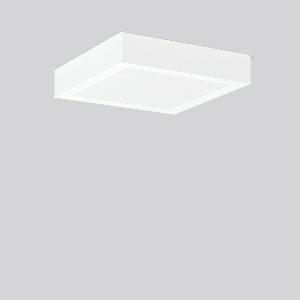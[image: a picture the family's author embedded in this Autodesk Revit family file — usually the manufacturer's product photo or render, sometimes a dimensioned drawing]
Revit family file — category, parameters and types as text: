
# Revit family: toledo_flat_square_a_672269_002_a995
name_source: partatom
category: Lighting Fixtures
units: mm (PartAtom-declared; Revit-internal decimal feet)

## family parameters
Cut with Voids When Loaded = No
Host = Face
Light Source = No
Part Type = Normal
Room Calculation Point = No
Round Connector Dimension = Use Diameter
Shared = No

## types (1)
- TOLEDO FLAT square A (1 x LED Modul 830, 2050 lm, 3000)
    Apparent Load = 22 VA
    CIE Flux Codes = 48 80 96 100 100
    Color Rendering = 80
    Color Temperature = 3000
    Default Elevation = 1800 mm
    Description = Series: TOLEDO FLAT square
Ultra thin surface mounted downlight. For escape route illumination. Surface mounted housing: sheet steel, powder-coated. Square cover plate: die-cast aluminium, powder coated. Light guide and diffuser made of non-yellowing PMMA, opal matt. Driver integrated. Suitable for connection to central battery systems. 
Colour: white
Length: 300 mm
Width: 300 mm
Height: 58 mm
Weight: 3.59 kg
Operating mode: maintained power mode
Lamp: LED
Socket: without socket
Colour temperature: 3000K
Colour rendering index (CRI): 80
System power: 22 W
Rated luminous flux: 2050 lm
Luminous flux, emergency: 2050 lm
System power, emergency: 22 W
Control gear: Regulated power supply
Protection class: I
Type of protection: IP 40
    Height = 58 mm
    Lamp = 1 x LED Modul 830
    Lamp Light Flux = 2050 lm
    Lamp count = 1
    Length = 300 mm
    Lifetime = 50000 h
    Luminous efficacy = 93 lm/W
    Manufacturer = RZB
    ModVariant = No
    Model = 672269.002
    Mounting Place = Ceiling
    Mounting Type = Surface mounted
    Number of Poles = 1
    OnlyDefault = Yes
    Power Factor = 1
    Product Name = TOLEDO FLAT square A
    Product group = Surface mounted downlights
    ProductGroupID = 302
    Protection Class = Protection class I
    Protection Degree = IP 40
    RLX_Detail_Level = 1
    RLX_Emergency_Light_Flux = 2050 lm
    RLX_Emergency_Type = 3
    RLX_Emergency_Type_DB = Yes
    RlxData = <blob elided: 13553 chars, md5=b06c832a>
    Socket = socket
    Standby Power = 0 W
    System Light Flux = 2050 lm
    System Power = 22 W
    Type Comments = Product without accessories
    Type Image = 901554.002.jpg
    URL = http://relux.com
    VarID = ---
    Voltage = 230 V
    Voltage Range = 220-240 V
    Weight = 0.00 kg
    Width = 300 mm

## geometry (parser evidence)
native form markers: Sweep x10
no freeform markers — native parametric forms only
